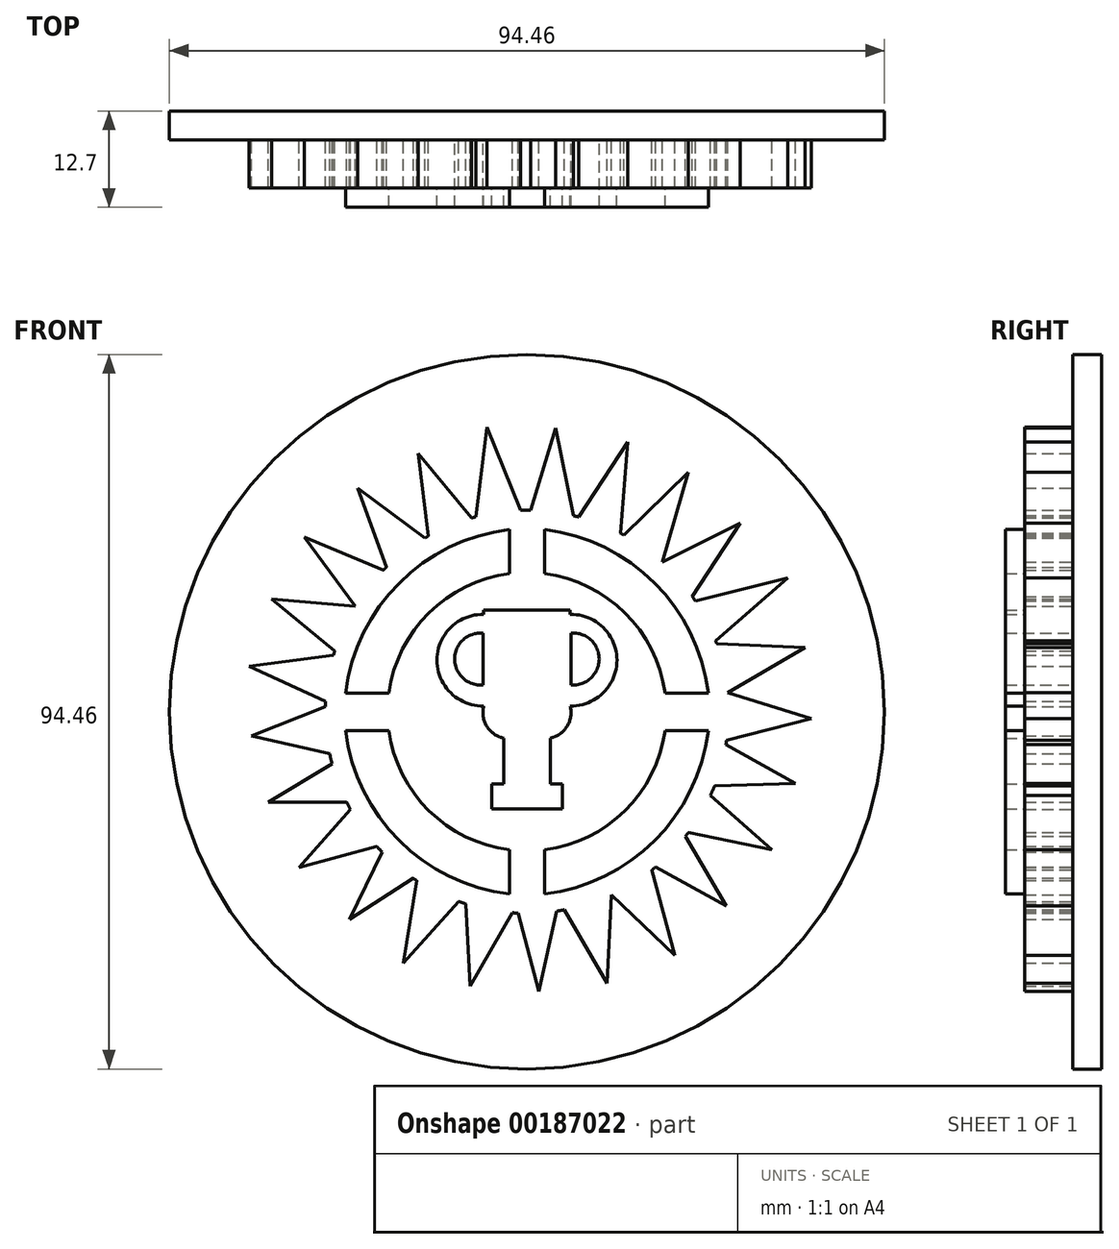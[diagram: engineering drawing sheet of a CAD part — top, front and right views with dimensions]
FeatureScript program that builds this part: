
annotation { "Feature Type Name" : "Feature", "Feature Type Description" : "" }
export const myFeature = defineFeature(function(context is Context, id is Id, definition is map)
    precondition{}
    {
        {
            var Q0;
            Q0=qCreatedBy(makeId("Front.planeOp"),FACE);
            var sketch = newSketch(context, id + "F0", { "sketchPlane" : qUnion([Q0])});
            skCircle(sketch, "E0", {"center": v(-38.3, 37.44) * mm, "radius": 26.65 * mm});
            skPoint(sketch, "E0.first.point", {"position": v(-25.5, 60.81) * mm});
            skPoint(sketch, "E0.second.point", {"position": v(-51.1, 14.07) * mm});
            skPoint(sketch, "E0.third.point", {"position": v(-62.96, 47.53) * mm});
            skLineSegment(sketch, "E1", {"start": v(-56.86, 56.56) * mm, "end": v(-60.63, 67.03) * mm});
            skLineSegment(sketch, "E2", {"start": v(-60.63, 67.03) * mm, "end": v(-51.75, 60.44) * mm});
            skLineSegment(sketch, "E3", {"start": v(-51.31, 60.7) * mm, "end": v(-52.68, 71.61) * mm});
            skLineSegment(sketch, "E4", {"start": v(-52.68, 71.61) * mm, "end": v(-45.61, 63.06) * mm});
            skLineSegment(sketch, "E5", {"start": v(-45.04, 63.22) * mm, "end": v(-43.6, 75.11) * mm});
            skLineSegment(sketch, "E6", {"start": v(-43.6, 75.11) * mm, "end": v(-39.16, 64.07) * mm});
            skLineSegment(sketch, "E7", {"start": v(-37.81, 64.08) * mm, "end": v(-34.49, 74.98) * mm});
            skLineSegment(sketch, "E8", {"start": v(-34.49, 74.98) * mm, "end": v(-32.18, 63.38) * mm});
            skLineSegment(sketch, "E9", {"start": v(-31.47, 63.2) * mm, "end": v(-24.97, 73.14) * mm});
            skLineSegment(sketch, "E10", {"start": v(-24.97, 73.14) * mm, "end": v(-25.94, 61.05) * mm});
            skLineSegment(sketch, "E11", {"start": v(-25.5, 60.81) * mm, "end": v(-16.97, 69.14) * mm});
            skLineSegment(sketch, "E12", {"start": v(-16.97, 69.14) * mm, "end": v(-20.44, 57.21) * mm});
            skLineSegment(sketch, "E13", {"start": v(-20.44, 57.21) * mm, "end": v(-10.1, 62.4) * mm});
            skLineSegment(sketch, "E14", {"start": v(-10.1, 62.4) * mm, "end": v(-16.45, 52.7) * mm});
            skLineSegment(sketch, "E15", {"start": v(-16.06, 52.11) * mm, "end": v(-3.8, 55.17) * mm});
            skLineSegment(sketch, "E16", {"start": v(-3.8, 55.17) * mm, "end": v(-13.36, 46.82) * mm});
            skLineSegment(sketch, "E17", {"start": v(-13.22, 46.43) * mm, "end": v(-1.52, 45.91) * mm});
            skLineSegment(sketch, "E18", {"start": v(-1.52, 45.91) * mm, "end": v(-11.77, 39.97) * mm});
            skLineSegment(sketch, "E19", {"start": v(-11.77, 39.97) * mm, "end": v(-0.75, 36.53) * mm});
            skLineSegment(sketch, "E20", {"start": v(-0.75, 36.53) * mm, "end": v(-11.91, 33.71) * mm});
            skLineSegment(sketch, "E21", {"start": v(-12.01, 33.09) * mm, "end": v(-2.8, 28) * mm});
            skLineSegment(sketch, "E22", {"start": v(-2.8, 28) * mm, "end": v(-13.51, 27.66) * mm});
            skLineSegment(sketch, "E23", {"start": v(-14.05, 26.4) * mm, "end": v(-5.94, 19.21) * mm});
            skLineSegment(sketch, "E24", {"start": v(-5.94, 19.21) * mm, "end": v(-16.95, 21.5) * mm});
            skLineSegment(sketch, "E25", {"start": v(-17.34, 20.99) * mm, "end": v(-11.96, 11.8) * mm});
            skLineSegment(sketch, "E26", {"start": v(-11.96, 11.8) * mm, "end": v(-21.32, 16.9) * mm});
            skLineSegment(sketch, "E27", {"start": v(-21.8, 16.52) * mm, "end": v(-18.79, 5.26) * mm});
            skLineSegment(sketch, "E28", {"start": v(-18.79, 5.26) * mm, "end": v(-27.16, 13.23) * mm});
            skLineSegment(sketch, "E29", {"start": v(-27.16, 13.23) * mm, "end": v(-27.7, 1.58) * mm});
            skLineSegment(sketch, "E30", {"start": v(-27.7, 1.58) * mm, "end": v(-33.36, 11.26) * mm});
            skLineSegment(sketch, "E31", {"start": v(-34.38, 11.09) * mm, "end": v(-36.72, 0.47) * mm});
            skLineSegment(sketch, "E32", {"start": v(-36.72, 0.47) * mm, "end": v(-39.44, 10.82) * mm});
            skLineSegment(sketch, "E33", {"start": v(-40.2, 10.86) * mm, "end": v(-45.8, 1.2) * mm});
            skLineSegment(sketch, "E34", {"start": v(-45.8, 1.2) * mm, "end": v(-46.4, 12.06) * mm});
            skLineSegment(sketch, "E35", {"start": v(-47.32, 12.37) * mm, "end": v(-54.66, 4.2) * mm});
            skLineSegment(sketch, "E36", {"start": v(-54.66, 4.2) * mm, "end": v(-52.85, 15.12) * mm});
            skLineSegment(sketch, "E37", {"start": v(-53.33, 15.44) * mm, "end": v(-61.74, 10.01) * mm});
            skLineSegment(sketch, "E38", {"start": v(-61.74, 10.01) * mm, "end": v(-57.45, 18.91) * mm});
            skLineSegment(sketch, "E39", {"start": v(-58.15, 19.66) * mm, "end": v(-68.44, 16.88) * mm});
            skLineSegment(sketch, "E40", {"start": v(-68.44, 16.88) * mm, "end": v(-61.62, 24.56) * mm});
            skLineSegment(sketch, "E41", {"start": v(-62.12, 25.5) * mm, "end": v(-72.47, 25.5) * mm});
            skLineSegment(sketch, "E42", {"start": v(-72.47, 25.5) * mm, "end": v(-64.05, 30.58) * mm});
            skLineSegment(sketch, "E43", {"start": v(-64.37, 31.93) * mm, "end": v(-74.67, 34.27) * mm});
            skLineSegment(sketch, "E44", {"start": v(-74.67, 34.27) * mm, "end": v(-64.94, 38.12) * mm});
            skLineSegment(sketch, "E45", {"start": v(-64.9, 38.84) * mm, "end": v(-75.01, 43.47) * mm});
            skLineSegment(sketch, "E46", {"start": v(-75.01, 43.47) * mm, "end": v(-63.88, 44.9) * mm});
            skLineSegment(sketch, "E47", {"start": v(-63.7, 45.5) * mm, "end": v(-72.04, 52.33) * mm});
            skLineSegment(sketch, "E48", {"start": v(-72.04, 52.33) * mm, "end": v(-61, 51.4) * mm});
            skLineSegment(sketch, "E49", {"start": v(-61, 51.4) * mm, "end": v(-67.72, 60.51) * mm});
            skLineSegment(sketch, "E50", {"start": v(-67.72, 60.51) * mm, "end": v(-57.24, 56.19) * mm});
            skArc(sketch, "E51", {"start": v(-56.55, 34.96) * mm, "mid": v(-51.25, 24.36) * mm, "end": v(-40.6, 19.18) * mm});
            skLineSegment(sketch, "E52", {"start": v(-40.6, 19.18) * mm, "end": v(-40.6, 13.34) * mm});
            skLineSegment(sketch, "E53", {"start": v(-56.55, 34.96) * mm, "end": v(-62.27, 34.96) * mm});
            skArc(sketch, "E54", {"start": v(-62.27, 34.96) * mm, "mid": v(-55.17, 20.41) * mm, "end": v(-40.6, 13.34) * mm});
            skLineSegment(sketch, "E55.MirrorCS", {"start": v(-36, 19.18) * mm, "end": v(-36, 13.34) * mm});
            skArc(sketch, "E56.MirrorCS", {"start": v(-20.05, 34.96) * mm, "mid": v(-25.35, 24.36) * mm, "end": v(-36, 19.18) * mm});
            skArc(sketch, "E57.MirrorCS", {"start": v(-14.32, 34.96) * mm, "mid": v(-21.43, 20.41) * mm, "end": v(-36, 13.34) * mm});
            skLineSegment(sketch, "E58.MirrorCS", {"start": v(-20.05, 34.96) * mm, "end": v(-14.32, 34.96) * mm});
            skLineSegment(sketch, "E59.MirrorCS", {"start": v(-56.55, 39.92) * mm, "end": v(-62.27, 39.92) * mm});
            skArc(sketch, "E60.MirrorCS", {"start": v(-56.55, 39.92) * mm, "mid": v(-51.25, 50.52) * mm, "end": v(-40.6, 55.7) * mm});
            skArc(sketch, "E61.MirrorCS", {"start": v(-62.27, 39.92) * mm, "mid": v(-55.17, 54.47) * mm, "end": v(-40.6, 61.54) * mm});
            skLineSegment(sketch, "E62.MirrorCS", {"start": v(-40.6, 55.7) * mm, "end": v(-40.6, 61.54) * mm});
            skLineSegment(sketch, "E63.MirrorCS", {"start": v(-36, 55.7) * mm, "end": v(-36, 61.54) * mm});
            skArc(sketch, "E64.MirrorCS", {"start": v(-20.05, 39.92) * mm, "mid": v(-25.35, 50.52) * mm, "end": v(-36, 55.7) * mm});
            skArc(sketch, "E65.MirrorCS", {"start": v(-14.32, 39.92) * mm, "mid": v(-21.43, 54.47) * mm, "end": v(-36, 61.54) * mm});
            skLineSegment(sketch, "E66.MirrorCS", {"start": v(-20.05, 39.92) * mm, "end": v(-14.32, 39.92) * mm});
            skLineSegment(sketch, "E67", {"start": v(-44.02, 50.91) * mm, "end": v(-38.3, 50.91) * mm});
            skLineSegment(sketch, "E68", {"start": v(-44.02, 50.91) * mm, "end": v(-44.02, 50.33) * mm});
            skArc(sketch, "E69", {"start": v(-44.02, 50.33) * mm, "mid": v(-50.19, 44.27) * mm, "end": v(-44.02, 38.22) * mm});
            skLineSegment(sketch, "E70", {"start": v(-44.1, 41) * mm, "end": v(-44.1, 47.86) * mm});
            skArc(sketch, "E71", {"start": v(-44.1, 47.86) * mm, "mid": v(-47.84, 44.42) * mm, "end": v(-44.1, 41) * mm});
            skLineSegment(sketch, "E72", {"start": v(-41.36, 27.92) * mm, "end": v(-41.36, 33.94) * mm});
            skArc(sketch, "E73", {"start": v(-44.02, 38.22) * mm, "mid": v(-43.6, 35.52) * mm, "end": v(-41.36, 33.94) * mm});
            skLineSegment(sketch, "E74", {"start": v(-41.36, 27.92) * mm, "end": v(-42.96, 27.92) * mm});
            skLineSegment(sketch, "E75", {"start": v(-42.96, 27.92) * mm, "end": v(-42.96, 24.61) * mm});
            skLineSegment(sketch, "E76", {"start": v(-42.96, 24.61) * mm, "end": v(-38.3, 24.61) * mm});
            skLineSegment(sketch, "E77.MirrorCS", {"start": v(-33.64, 24.61) * mm, "end": v(-38.3, 24.61) * mm});
            skLineSegment(sketch, "E78.MirrorCS", {"start": v(-33.64, 27.92) * mm, "end": v(-33.64, 24.61) * mm});
            skLineSegment(sketch, "E79.MirrorCS", {"start": v(-35.24, 27.92) * mm, "end": v(-33.64, 27.92) * mm});
            skLineSegment(sketch, "E80.MirrorCS", {"start": v(-35.24, 27.92) * mm, "end": v(-35.24, 33.94) * mm});
            skArc(sketch, "E81.MirrorCS", {"start": v(-32.58, 38.22) * mm, "mid": v(-33, 35.52) * mm, "end": v(-35.24, 33.94) * mm});
            skArc(sketch, "E82.MirrorCS", {"start": v(-32.58, 50.33) * mm, "mid": v(-26.4, 44.27) * mm, "end": v(-32.58, 38.22) * mm});
            skArc(sketch, "E83.MirrorCS", {"start": v(-32.5, 47.86) * mm, "mid": v(-28.75, 44.42) * mm, "end": v(-32.5, 41) * mm});
            skLineSegment(sketch, "E84.MirrorCS", {"start": v(-32.5, 41) * mm, "end": v(-32.5, 47.86) * mm});
            skLineSegment(sketch, "E85.MirrorCS", {"start": v(-32.58, 50.91) * mm, "end": v(-32.58, 50.33) * mm});
            skLineSegment(sketch, "E86.MirrorCS", {"start": v(-32.58, 50.91) * mm, "end": v(-38.3, 50.91) * mm});
            skSolve(sketch);
        }
        {
            var Q0;
            {var subQ0=sQuery(id+"F0.wireOp",EDGE,"E41");Q0=makeQuery(id+"F0.imprint","IMPRINT",FACE,{"disambiguationData":[TD([[makeQuery(id+"F0.imprint","IMPRINT",EDGE,{"derivedFrom":subQ0}),-1.0]])]});}
            var Q1;
            {var subQ0=sQuery(id+"F0.wireOp",EDGE,"E39");Q1=makeQuery(id+"F0.imprint","IMPRINT",FACE,{"disambiguationData":[TD([[makeQuery(id+"F0.imprint","IMPRINT",EDGE,{"derivedFrom":subQ0}),-1.0]])]});}
            var Q2;
            {var subQ0=sQuery(id+"F0.wireOp",EDGE,"E37");Q2=makeQuery(id+"F0.imprint","IMPRINT",FACE,{"disambiguationData":[TD([[makeQuery(id+"F0.imprint","IMPRINT",EDGE,{"derivedFrom":subQ0}),-1.0]])]});}
            var Q3;
            {var subQ0=sQuery(id+"F0.wireOp",EDGE,"E35");Q3=makeQuery(id+"F0.imprint","IMPRINT",FACE,{"disambiguationData":[TD([[makeQuery(id+"F0.imprint","IMPRINT",EDGE,{"derivedFrom":subQ0}),-1.0]])]});}
            var Q4;
            {var subQ0=sQuery(id+"F0.wireOp",EDGE,"E33");Q4=makeQuery(id+"F0.imprint","IMPRINT",FACE,{"disambiguationData":[TD([[makeQuery(id+"F0.imprint","IMPRINT",EDGE,{"derivedFrom":subQ0}),-1.0]])]});}
            var Q5;
            {var subQ0=sQuery(id+"F0.wireOp",EDGE,"E29");Q5=makeQuery(id+"F0.imprint","IMPRINT",FACE,{"disambiguationData":[TD([[makeQuery(id+"F0.imprint","IMPRINT",EDGE,{"derivedFrom":subQ0}),-1.0]])]});}
            var Q6;
            {var subQ0=sQuery(id+"F0.wireOp",EDGE,"E31");Q6=makeQuery(id+"F0.imprint","IMPRINT",FACE,{"disambiguationData":[TD([[makeQuery(id+"F0.imprint","IMPRINT",EDGE,{"derivedFrom":subQ0}),-1.0]])]});}
            var Q7;
            {var subQ0=sQuery(id+"F0.wireOp",EDGE,"E27");Q7=makeQuery(id+"F0.imprint","IMPRINT",FACE,{"disambiguationData":[TD([[makeQuery(id+"F0.imprint","IMPRINT",EDGE,{"derivedFrom":subQ0}),-1.0]])]});}
            var Q8;
            {var subQ0=sQuery(id+"F0.wireOp",EDGE,"E25");Q8=makeQuery(id+"F0.imprint","IMPRINT",FACE,{"disambiguationData":[TD([[makeQuery(id+"F0.imprint","IMPRINT",EDGE,{"derivedFrom":subQ0}),-1.0]])]});}
            var Q9;
            {var subQ0=sQuery(id+"F0.wireOp",EDGE,"E23");Q9=makeQuery(id+"F0.imprint","IMPRINT",FACE,{"disambiguationData":[TD([[makeQuery(id+"F0.imprint","IMPRINT",EDGE,{"derivedFrom":subQ0}),-1.0]])]});}
            var Q10;
            {var subQ0=sQuery(id+"F0.wireOp",EDGE,"E21");Q10=makeQuery(id+"F0.imprint","IMPRINT",FACE,{"disambiguationData":[TD([[makeQuery(id+"F0.imprint","IMPRINT",EDGE,{"derivedFrom":subQ0}),-1.0]])]});}
            var Q11;
            {var subQ0=sQuery(id+"F0.wireOp",EDGE,"E19");Q11=makeQuery(id+"F0.imprint","IMPRINT",FACE,{"disambiguationData":[TD([[makeQuery(id+"F0.imprint","IMPRINT",EDGE,{"derivedFrom":subQ0}),-1.0]])]});}
            var Q12;
            {var subQ0=sQuery(id+"F0.wireOp",EDGE,"E17");Q12=makeQuery(id+"F0.imprint","IMPRINT",FACE,{"disambiguationData":[TD([[makeQuery(id+"F0.imprint","IMPRINT",EDGE,{"derivedFrom":subQ0}),-1.0]])]});}
            var Q13;
            {var subQ0=sQuery(id+"F0.wireOp",EDGE,"E15");Q13=makeQuery(id+"F0.imprint","IMPRINT",FACE,{"disambiguationData":[TD([[makeQuery(id+"F0.imprint","IMPRINT",EDGE,{"derivedFrom":subQ0}),-1.0]])]});}
            var Q14;
            {var subQ0=sQuery(id+"F0.wireOp",EDGE,"E13");Q14=makeQuery(id+"F0.imprint","IMPRINT",FACE,{"disambiguationData":[TD([[makeQuery(id+"F0.imprint","IMPRINT",EDGE,{"derivedFrom":subQ0}),-1.0]])]});}
            var Q15;
            {var subQ0=sQuery(id+"F0.wireOp",EDGE,"E11");Q15=makeQuery(id+"F0.imprint","IMPRINT",FACE,{"disambiguationData":[TD([[makeQuery(id+"F0.imprint","IMPRINT",EDGE,{"derivedFrom":subQ0}),-1.0]])]});}
            var Q16;
            {var subQ0=sQuery(id+"F0.wireOp",EDGE,"E9");Q16=makeQuery(id+"F0.imprint","IMPRINT",FACE,{"disambiguationData":[TD([[makeQuery(id+"F0.imprint","IMPRINT",EDGE,{"derivedFrom":subQ0}),-1.0]])]});}
            var Q17;
            {var subQ0=sQuery(id+"F0.wireOp",EDGE,"E7");Q17=makeQuery(id+"F0.imprint","IMPRINT",FACE,{"disambiguationData":[TD([[makeQuery(id+"F0.imprint","IMPRINT",EDGE,{"derivedFrom":subQ0}),-1.0]])]});}
            var Q18;
            {var subQ0=sQuery(id+"F0.wireOp",EDGE,"E5");Q18=makeQuery(id+"F0.imprint","IMPRINT",FACE,{"disambiguationData":[TD([[makeQuery(id+"F0.imprint","IMPRINT",EDGE,{"derivedFrom":subQ0}),-1.0]])]});}
            var Q19;
            {var subQ0=sQuery(id+"F0.wireOp",EDGE,"E3");Q19=makeQuery(id+"F0.imprint","IMPRINT",FACE,{"disambiguationData":[TD([[makeQuery(id+"F0.imprint","IMPRINT",EDGE,{"derivedFrom":subQ0}),-1.0]])]});}
            var Q20;
            {var subQ0=sQuery(id+"F0.wireOp",EDGE,"E1");Q20=makeQuery(id+"F0.imprint","IMPRINT",FACE,{"disambiguationData":[TD([[makeQuery(id+"F0.imprint","IMPRINT",EDGE,{"derivedFrom":subQ0}),-1.0]])]});}
            var Q21;
            {var subQ0=sQuery(id+"F0.wireOp",EDGE,"E49");Q21=makeQuery(id+"F0.imprint","IMPRINT",FACE,{"disambiguationData":[TD([[makeQuery(id+"F0.imprint","IMPRINT",EDGE,{"derivedFrom":subQ0}),-1.0]])]});}
            var Q22;
            {var subQ0=sQuery(id+"F0.wireOp",EDGE,"E47");Q22=makeQuery(id+"F0.imprint","IMPRINT",FACE,{"disambiguationData":[TD([[makeQuery(id+"F0.imprint","IMPRINT",EDGE,{"derivedFrom":subQ0}),-1.0]])]});}
            var Q23;
            {var subQ0=sQuery(id+"F0.wireOp",EDGE,"E45");Q23=makeQuery(id+"F0.imprint","IMPRINT",FACE,{"disambiguationData":[TD([[makeQuery(id+"F0.imprint","IMPRINT",EDGE,{"derivedFrom":subQ0}),-1.0]])]});}
            var Q24;
            {var subQ0=sQuery(id+"F0.wireOp",EDGE,"E43");Q24=makeQuery(id+"F0.imprint","IMPRINT",FACE,{"disambiguationData":[TD([[makeQuery(id+"F0.imprint","IMPRINT",EDGE,{"derivedFrom":subQ0}),-1.0]])]});}
            var Q25;
            Q25=makeQuery(id+"F0.imprint","IMPRINT",FACE,{"disambiguationData":[TD([[makeQuery(id+"F0.imprint","IMPRINT",EDGE,{"derivedFrom":sQuery(id+"F0.wireOp",EDGE,"E51")}),1.0]])]});
            extrude(context, id + "F1", {"entities" : qUnion([Q0, Q1, Q2, Q3, Q4, Q5, Q6, Q7, Q8, Q9, Q10, Q11, Q12, Q13, Q14, Q15, Q16, Q17, Q18, Q19, Q20, Q21, Q22, Q23, Q24, Q25]), "depth" : 6.35 * mm});
        }
        {
            var Q0;
            Q0=makeQuery(id+"F0.imprint","IMPRINT",FACE,{"disambiguationData":[TD([[makeQuery(id+"F0.imprint","IMPRINT",EDGE,{"derivedFrom":sQuery(id+"F0.wireOp",EDGE,"E51")}),-1.0]])]});
            var Q1;
            Q1=makeQuery(id+"F0.imprint","IMPRINT",FACE,{"disambiguationData":[TD([[makeQuery(id+"F0.imprint","IMPRINT",EDGE,{"derivedFrom":sQuery(id+"F0.wireOp",EDGE,"E55.MirrorCS")}),1.0]])]});
            var Q2;
            Q2=makeQuery(id+"F0.imprint","IMPRINT",FACE,{"disambiguationData":[TD([[makeQuery(id+"F0.imprint","IMPRINT",EDGE,{"derivedFrom":sQuery(id+"F0.wireOp",EDGE,"E64.MirrorCS")}),-1.0]])]});
            var Q3;
            Q3=makeQuery(id+"F0.imprint","IMPRINT",FACE,{"disambiguationData":[TD([[makeQuery(id+"F0.imprint","IMPRINT",EDGE,{"derivedFrom":sQuery(id+"F0.wireOp",EDGE,"E59.MirrorCS")}),-1.0]])]});
            var Q4;
            Q4=makeQuery(id+"F0.imprint","IMPRINT",FACE,{"disambiguationData":[TD([[makeQuery(id+"F0.imprint","IMPRINT",EDGE,{"derivedFrom":sQuery(id+"F0.wireOp",EDGE,"E67")}),-1.0]])]});
            extrude(context, id + "F2", {"entities" : qUnion([Q0, Q1, Q2, Q3, Q4]), "operationType" : NewBodyOperationType.ADD, "depth" : 8.9 * mm});
        }
        {
            var Q0;
            {var subQ0=sQuery(id+"F0.wireOp",EDGE,"E86.MirrorCS");var subQ1=sQuery(id+"F0.wireOp",EDGE,"E85.MirrorCS");var subQ2=sQuery(id+"F0.wireOp",EDGE,"E82.MirrorCS");var subQ3=sQuery(id+"F0.wireOp",EDGE,"E81.MirrorCS");var subQ4=sQuery(id+"F0.wireOp",EDGE,"E80.MirrorCS");var subQ5=sQuery(id+"F0.wireOp",EDGE,"E79.MirrorCS");var subQ6=sQuery(id+"F0.wireOp",EDGE,"E78.MirrorCS");var subQ7=sQuery(id+"F0.wireOp",EDGE,"E77.MirrorCS");var subQ8=sQuery(id+"F0.wireOp",EDGE,"E76");var subQ9=sQuery(id+"F0.wireOp",EDGE,"E75");var subQ10=sQuery(id+"F0.wireOp",EDGE,"E74");var subQ11=sQuery(id+"F0.wireOp",EDGE,"E73");var subQ12=sQuery(id+"F0.wireOp",EDGE,"E72");var subQ13=sQuery(id+"F0.wireOp",EDGE,"E69");var subQ14=sQuery(id+"F0.wireOp",EDGE,"E68");var subQ15=sQuery(id+"F0.wireOp",EDGE,"E67");var subQ16=sQuery(id+"F0.wireOp",EDGE,"E66.MirrorCS");var subQ17=sQuery(id+"F0.wireOp",EDGE,"E63.MirrorCS");var subQ18=sQuery(id+"F0.wireOp",EDGE,"E65.MirrorCS");var subQ19=sQuery(id+"F0.wireOp",EDGE,"E64.MirrorCS");var subQ20=sQuery(id+"F0.wireOp",EDGE,"E62.MirrorCS");var subQ21=sQuery(id+"F0.wireOp",EDGE,"E61.MirrorCS");var subQ22=sQuery(id+"F0.wireOp",EDGE,"E60.MirrorCS");var subQ23=sQuery(id+"F0.wireOp",EDGE,"E59.MirrorCS");var subQ24=sQuery(id+"F0.wireOp",EDGE,"E58.MirrorCS");var subQ25=sQuery(id+"F0.wireOp",EDGE,"E57.MirrorCS");var subQ26=sQuery(id+"F0.wireOp",EDGE,"E56.MirrorCS");var subQ27=sQuery(id+"F0.wireOp",EDGE,"E55.MirrorCS");var subQ28=sQuery(id+"F0.wireOp",EDGE,"E54");var subQ29=sQuery(id+"F0.wireOp",EDGE,"E53");var subQ30=sQuery(id+"F0.wireOp",EDGE,"E52");var subQ31=sQuery(id+"F0.wireOp",EDGE,"E51");Q0=makeQuery(id+"F2.boolean.opBoolean","MERGE",FACE,{"derivedFrom":[makeQuery(id+"F1.opExtrude","CAP_FACE",FACE,{"disambiguationData":[OSD([sQuery(id+"F0.wireOp",EDGE,"E0"),sQuery(id+"F0.wireOp",EDGE,"E1"),sQuery(id+"F0.wireOp",EDGE,"E2"),sQuery(id+"F0.wireOp",EDGE,"E3"),sQuery(id+"F0.wireOp",EDGE,"E4"),sQuery(id+"F0.wireOp",EDGE,"E5"),sQuery(id+"F0.wireOp",EDGE,"E6"),sQuery(id+"F0.wireOp",EDGE,"E7"),sQuery(id+"F0.wireOp",EDGE,"E8"),sQuery(id+"F0.wireOp",EDGE,"E9"),sQuery(id+"F0.wireOp",EDGE,"E10"),sQuery(id+"F0.wireOp",EDGE,"E11"),sQuery(id+"F0.wireOp",EDGE,"E12"),sQuery(id+"F0.wireOp",EDGE,"E13"),sQuery(id+"F0.wireOp",EDGE,"E14"),sQuery(id+"F0.wireOp",EDGE,"E15"),sQuery(id+"F0.wireOp",EDGE,"E16"),sQuery(id+"F0.wireOp",EDGE,"E17"),sQuery(id+"F0.wireOp",EDGE,"E18"),sQuery(id+"F0.wireOp",EDGE,"E19"),sQuery(id+"F0.wireOp",EDGE,"E20"),sQuery(id+"F0.wireOp",EDGE,"E21"),sQuery(id+"F0.wireOp",EDGE,"E22"),sQuery(id+"F0.wireOp",EDGE,"E23"),sQuery(id+"F0.wireOp",EDGE,"E24"),sQuery(id+"F0.wireOp",EDGE,"E25"),sQuery(id+"F0.wireOp",EDGE,"E26"),sQuery(id+"F0.wireOp",EDGE,"E27"),sQuery(id+"F0.wireOp",EDGE,"E28"),sQuery(id+"F0.wireOp",EDGE,"E29"),sQuery(id+"F0.wireOp",EDGE,"E30"),sQuery(id+"F0.wireOp",EDGE,"E31"),sQuery(id+"F0.wireOp",EDGE,"E32"),sQuery(id+"F0.wireOp",EDGE,"E33"),sQuery(id+"F0.wireOp",EDGE,"E34"),sQuery(id+"F0.wireOp",EDGE,"E35"),sQuery(id+"F0.wireOp",EDGE,"E36"),sQuery(id+"F0.wireOp",EDGE,"E37"),sQuery(id+"F0.wireOp",EDGE,"E38"),sQuery(id+"F0.wireOp",EDGE,"E39"),sQuery(id+"F0.wireOp",EDGE,"E40"),sQuery(id+"F0.wireOp",EDGE,"E41"),sQuery(id+"F0.wireOp",EDGE,"E42"),sQuery(id+"F0.wireOp",EDGE,"E43"),sQuery(id+"F0.wireOp",EDGE,"E44"),sQuery(id+"F0.wireOp",EDGE,"E45"),sQuery(id+"F0.wireOp",EDGE,"E46"),sQuery(id+"F0.wireOp",EDGE,"E47"),sQuery(id+"F0.wireOp",EDGE,"E48"),sQuery(id+"F0.wireOp",EDGE,"E49"),sQuery(id+"F0.wireOp",EDGE,"E50"),subQ31,subQ30,subQ29,subQ28,subQ27,subQ26,subQ25,subQ24,subQ23,subQ22,subQ21,subQ20,subQ19,subQ18,subQ17,subQ16,subQ15,subQ14,subQ13,subQ12,subQ11,subQ10,subQ9,subQ8,subQ7,subQ6,subQ5,subQ4,subQ3,subQ2,subQ1,subQ0])],"isStart":true}),makeQuery(id+"F2.opExtrude","CAP_FACE",FACE,{"disambiguationData":[OSD([subQ31,subQ30,subQ29,subQ28])],"isStart":true}),makeQuery(id+"F2.opExtrude","CAP_FACE",FACE,{"disambiguationData":[OSD([subQ27,subQ26,subQ25,subQ24])],"isStart":true}),makeQuery(id+"F2.opExtrude","CAP_FACE",FACE,{"disambiguationData":[OSD([subQ23,subQ22,subQ21,subQ20])],"isStart":true}),makeQuery(id+"F2.opExtrude","CAP_FACE",FACE,{"disambiguationData":[OSD([subQ19,subQ18,subQ17,subQ16])],"isStart":true}),makeQuery(id+"F2.opExtrude","CAP_FACE",FACE,{"disambiguationData":[OSD([subQ15,subQ14,subQ13,sQuery(id+"F0.wireOp",EDGE,"E70"),sQuery(id+"F0.wireOp",EDGE,"E71"),subQ12,subQ11,subQ10,subQ9,subQ8,subQ7,subQ6,subQ5,subQ4,subQ3,subQ2,sQuery(id+"F0.wireOp",EDGE,"E83.MirrorCS"),sQuery(id+"F0.wireOp",EDGE,"E84.MirrorCS"),subQ1,subQ0])],"isStart":true})]});}
            var sketch = newSketch(context, id + "F3", { "sketchPlane" : qUnion([Q0])});
            skCircle(sketch, "E87", {"center": v(38.3, 37.44) * mm, "radius": 47.23 * mm});
            skSolve(sketch);
        }
        {
            var Q0;
            Q0 = qSketchRegion(id + "F3", true);
            extrude(context, id + "F4", {"entities" : qUnion([Q0]), "operationType" : NewBodyOperationType.ADD, "depth" : 3.8 * mm});
        }
    });
